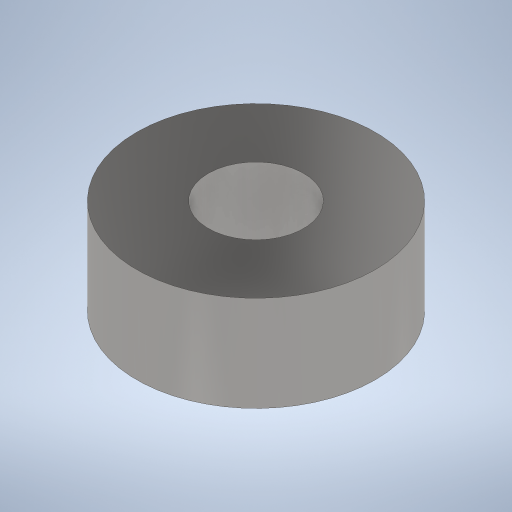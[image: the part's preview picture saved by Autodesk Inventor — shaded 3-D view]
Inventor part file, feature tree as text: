
AUTODESK INVENTOR PART (.ipt)
format: ipt  version: 2023.1 (Build 271208000, 208)  size: 227,840 bytes
history: native  units: mm
features: extrude x1, sketch x1
ambient origin geometry x8: Origin, YZ Plane, XZ Plane, XY Plane, X Axis, Y Axis, Z Axis, Center Point
bodies: Solid1 (feature_tree)
feature tree (2):
  extrude  "Extrusion1"  Depth=10.0mm
  sketch  "Sketch1"  dims[d0=4.0mm d1=10.0mm d2=4.0mm d3=0.0mm]
